# Revit family: Plumbing-Sink-Sloan-Valve-ESS-3200
name_source: partatom
category: Plumbing Fixtures
units: mm (PartAtom-declared; Revit-internal decimal feet)

## family parameters
Cut with Voids When Loaded = No
Host = Face
OmniClass Number = 23.45.05.14.14
OmniClass Title = Sinks/Lavatories
Part Type = Normal
Room Calculation Point = No
Round Connector Dimension = Use Diameter
Shared = No

## types (2) — shared parameters
ADA Compliant = Yes
Apparent Load = 688 VA
Assembly Code = D2010400
CW Connection = Yes
CWFU = 3
Cold Water Connection Diameter = 0.5 "
Current = 15 A
Depth = 25.31 "
Description = Stainless Steel 2-Station Wall-Mounted Deluxe Scrub Sink.
Edition number = 1
Frequency = 60 Hz
HW Connection = Yes
HWFU = 3
Height = 39.5 "
Hot Water Connection Diameter = 0.5 "
Keynote = 10000
Manufacturer = Sloan Valve
Number of Poles = 3
Power Factor = 0.8
Product Material = Sloan Valve - Finish - Stainless Steel
Product data url = https://bimobject.com
Sanitary Drain Connection Diameter = 1.5 "
URL = www.sloanvalve.com
Valve Pressure Drop = 0.0 Pa
Vent Connection = No
Voltage = 110 V
WFU = 3
Waste Connection = Yes
Water Flow = 2.2 GPM
Width = 64 "
zero-valued in all types: Default Elevation

## per-type parameters (varying)
| type | Part Number | z_C | z_Mixer |
| ESS-3200 |  | No | No |
| ESS-3200-C-ADM | 3850215 | Yes | Yes |

note: column(s) folded — value = type name in every type: Model

## geometry (parser evidence)
native form markers: Sweep x7
no freeform markers — native parametric forms only
